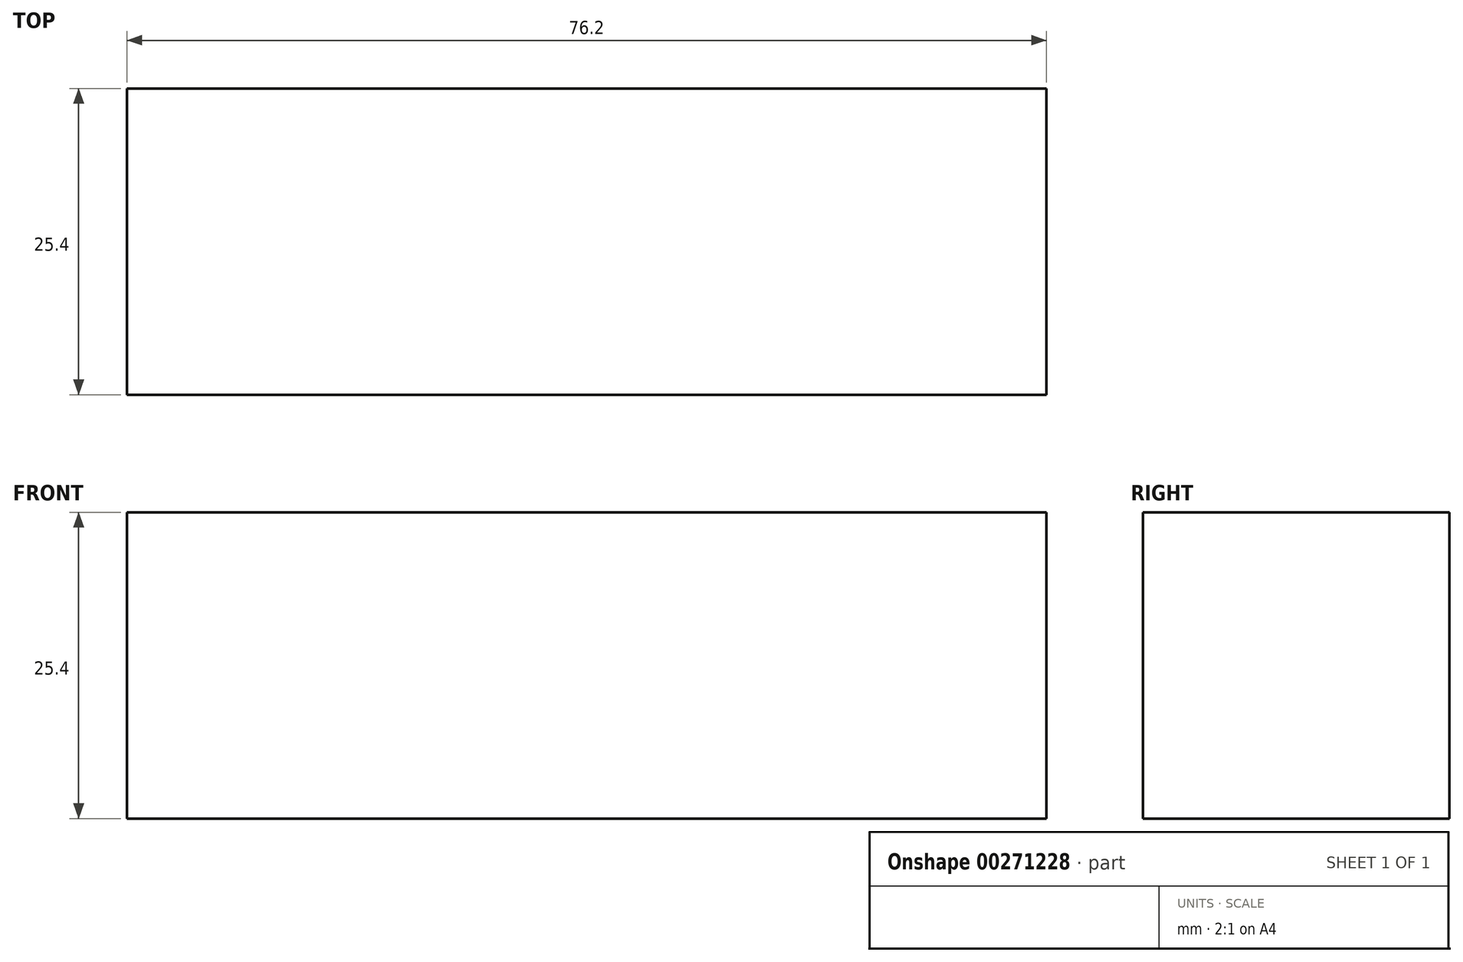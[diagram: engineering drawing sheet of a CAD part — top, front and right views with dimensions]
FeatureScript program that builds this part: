
annotation { "Feature Type Name" : "Feature", "Feature Type Description" : "" }
export const myFeature = defineFeature(function(context is Context, id is Id, definition is map)
    precondition{}
    {
        {
            var Q0;
            Q0=qCreatedBy(makeId("Front.planeOp"),FACE);
            var sketch = newSketch(context, id + "F0", { "sketchPlane" : qUnion([Q0])});
            skLineSegment(sketch, "E0.bottom", {"start": v(0, 0) * mm, "end": v(76.2, 0) * mm});
            skLineSegment(sketch, "E0.top", {"start": v(0, 25.4) * mm, "end": v(76.2, 25.4) * mm});
            skLineSegment(sketch, "E0.left", {"start": v(0, 0) * mm, "end": v(0, 25.4) * mm});
            skLineSegment(sketch, "E0.right", {"start": v(76.2, 0) * mm, "end": v(76.2, 25.4) * mm});
            skLineSegment(sketch, "E1.bottom", {"start": v(24.76, 25.4) * mm, "end": v(50.16, 25.4) * mm});
            skLineSegment(sketch, "E1.top", {"start": v(24.76, 76.2) * mm, "end": v(50.16, 76.2) * mm});
            skLineSegment(sketch, "E1.left", {"start": v(24.76, 25.4) * mm, "end": v(24.76, 76.2) * mm});
            skLineSegment(sketch, "E1.right", {"start": v(50.16, 25.4) * mm, "end": v(50.16, 76.2) * mm});
            skSolve(sketch);
        }
        {
            var Q0;
            Q0=makeQuery(id+"F0.imprint","IMPRINT",FACE,{"disambiguationData":[TD([[makeQuery(id+"F0.imprint","IMPRINT",EDGE,{"derivedFrom":sQuery(id+"F0.wireOp",EDGE,"E0.bottom")}),1.0]])]});
            var Q1;
            Q1=makeQuery(id+"F0.imprint","IMPRINT",FACE,{"disambiguationData":[TD([[makeQuery(id+"F0.imprint","IMPRINT",EDGE,{"derivedFrom":sQuery(id+"F0.wireOp",EDGE,"E1.bottom")}),1.0]])]});
            extrude(context, id + "F1", {"entities" : qUnion([Q0, Q1]), "depth" : 25.4 * mm});
        }
    });
